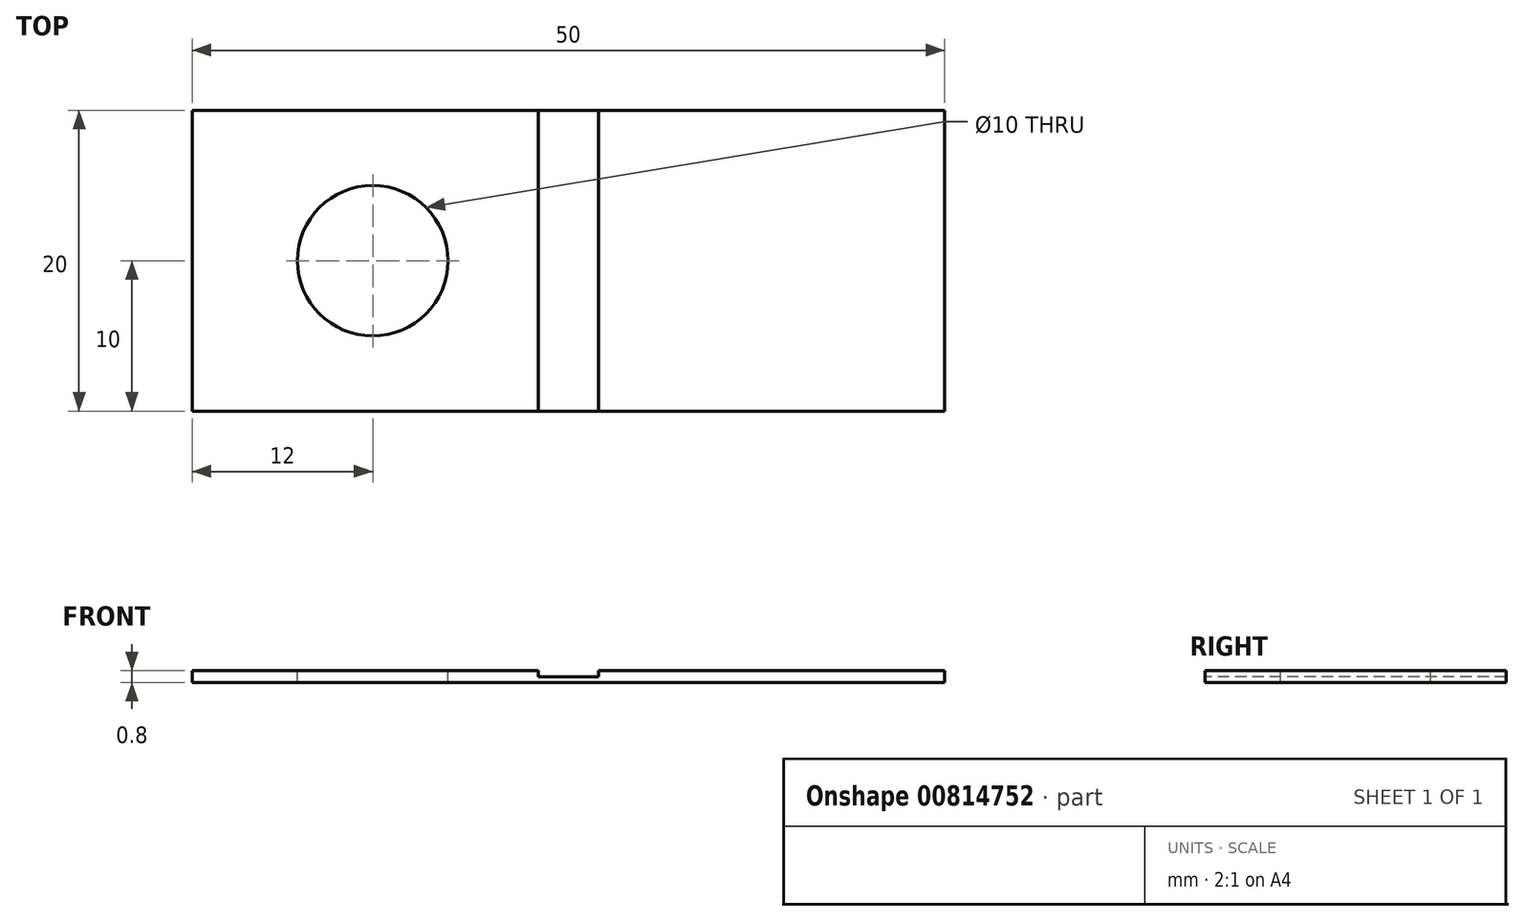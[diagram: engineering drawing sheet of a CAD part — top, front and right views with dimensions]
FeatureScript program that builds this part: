
annotation { "Feature Type Name" : "Feature", "Feature Type Description" : "" }
export const myFeature = defineFeature(function(context is Context, id is Id, definition is map)
    precondition{}
    {
        {
            var Q0;
            Q0=qCreatedBy(makeId("Top.planeOp"),FACE);
            var sketch = newSketch(context, id + "F0", { "sketchPlane" : qUnion([Q0])});
            skLineSegment(sketch, "E0.bottom", {"start": v(-25, 10) * mm, "end": v(25, 10) * mm});
            skLineSegment(sketch, "E0.top", {"start": v(-25, -10) * mm, "end": v(25, -10) * mm});
            skLineSegment(sketch, "E0.left", {"start": v(-25, 10) * mm, "end": v(-25, -10) * mm});
            skLineSegment(sketch, "E0.right", {"start": v(25, 10) * mm, "end": v(25, -10) * mm});
            skPoint(sketch, "E0.middle", {"position": v(0, 0) * mm});
            skSolve(sketch);
        }
        {
            var Q0;
            Q0=makeQuery(id+"F0.imprint","IMPRINT",FACE,{"disambiguationData":[TD([[makeQuery(id+"F0.imprint","IMPRINT",EDGE,{"derivedFrom":sQuery(id+"F0.wireOp",EDGE,"E0.bottom")}),-1.0]])]});
            extrude(context, id + "F1", {"entities" : qUnion([Q0]), "depth" : 0.4 * mm, "offsetDistance" : 25 * mm});
        }
        {
            var Q0;
            Q0=makeQuery(id+"F1.opExtrude","CAP_FACE",FACE,{"disambiguationData":[OSD([sQuery(id+"F0.wireOp",EDGE,"E0.bottom"),sQuery(id+"F0.wireOp",EDGE,"E0.top"),sQuery(id+"F0.wireOp",EDGE,"E0.left"),sQuery(id+"F0.wireOp",EDGE,"E0.right")])],"isStart":false});
            var sketch = newSketch(context, id + "F2", { "sketchPlane" : qUnion([Q0])});
            skLineSegment(sketch, "E1.bottom", {"start": v(-25, 10) * mm, "end": v(25, 10) * mm});
            skLineSegment(sketch, "E1.top", {"start": v(-25, -10) * mm, "end": v(25, -10) * mm});
            skLineSegment(sketch, "E1.left", {"start": v(-25, 10) * mm, "end": v(-25, -10) * mm});
            skLineSegment(sketch, "E1.right", {"start": v(25, 10) * mm, "end": v(25, -10) * mm});
            skLineSegment(sketch, "E2.left", {"start": v(-2, 10) * mm, "end": v(-2, -10) * mm});
            skLineSegment(sketch, "E2.right", {"start": v(2, 10) * mm, "end": v(2, -10) * mm});
            skSolve(sketch);
        }
        {
            var Q0;
            {var subQ0=sQuery(id+"F2.wireOp",EDGE,"E1.left");Q0=makeQuery(id+"F2.imprint","IMPRINT",FACE,{"disambiguationData":[TD([[makeQuery(id+"F2.imprint","IMPRINT",EDGE,{"derivedFrom":subQ0}),1.0]])]});}
            var Q1;
            {var subQ0=sQuery(id+"F2.wireOp",EDGE,"E1.right");Q1=makeQuery(id+"F2.imprint","IMPRINT",FACE,{"disambiguationData":[TD([[makeQuery(id+"F2.imprint","IMPRINT",EDGE,{"derivedFrom":subQ0}),-1.0]])]});}
            extrude(context, id + "F3", {"entities" : qUnion([Q0, Q1]), "operationType" : NewBodyOperationType.ADD, "depth" : 0.4 * mm, "offsetDistance" : 25 * mm});
        }
        {
            var Q0;
            Q0=makeQuery(id+"F3.opExtrude","CAP_FACE",FACE,{"disambiguationData":[OSD([sQuery(id+"F2.wireOp",EDGE,"E1.bottom"),sQuery(id+"F2.wireOp",EDGE,"E1.top"),sQuery(id+"F2.wireOp",EDGE,"E1.left"),sQuery(id+"F2.wireOp",EDGE,"E2.left")])],"isStart":false});
            var sketch = newSketch(context, id + "F4", { "sketchPlane" : qUnion([Q0])});
            skCircle(sketch, "E3", {"center": v(-13, 0) * mm, "radius": 5 * mm});
            skSolve(sketch);
        }
        {
            var Q0;
            Q0=makeQuery(id+"F4.imprint","IMPRINT",FACE,{"disambiguationData":[TD([[makeQuery(id+"F4.imprint","IMPRINT",EDGE,{"derivedFrom":sQuery(id+"F4.wireOp",EDGE,"E3")}),1.0]])]});
            extrude(context, id + "F5", {"entities" : qUnion([Q0]), "operationType" : NewBodyOperationType.REMOVE, "oppositeDirection" : true, "depth" : 25 * mm, "offsetDistance" : 25 * mm});
        }
    });
